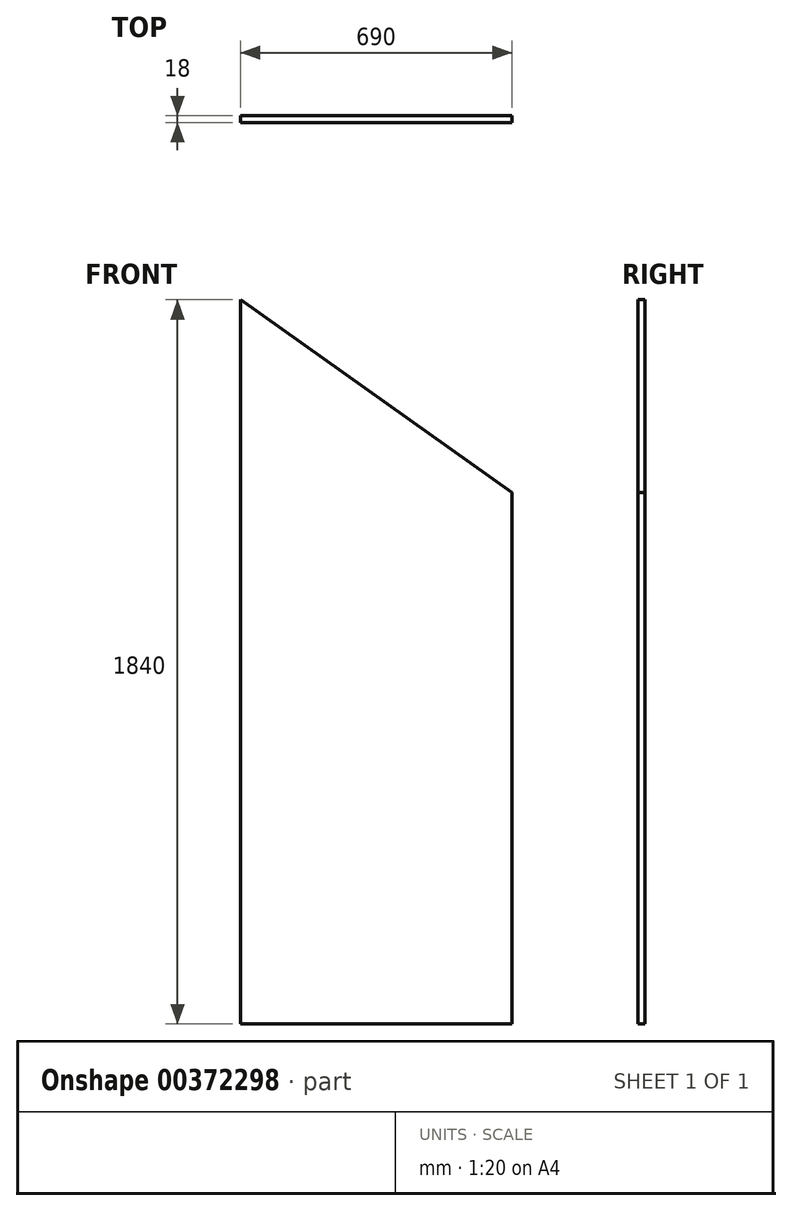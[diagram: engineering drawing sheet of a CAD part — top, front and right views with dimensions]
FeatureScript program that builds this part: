
annotation { "Feature Type Name" : "Feature", "Feature Type Description" : "" }
export const myFeature = defineFeature(function(context is Context, id is Id, definition is map)
    precondition{}
    {
        {
            var Q0;
            Q0=qCreatedBy(makeId("Front.planeOp"),FACE);
            var sketch = newSketch(context, id + "F0", { "sketchPlane" : qUnion([Q0])});
            skLineSegment(sketch, "E0", {"start": v(0, 0) * mm, "end": v(0, 1840) * mm});
            skLineSegment(sketch, "E1", {"start": v(0, 1840) * mm, "end": v(690, 1350) * mm});
            skLineSegment(sketch, "E2", {"start": v(690, 1350) * mm, "end": v(690, 0) * mm});
            skLineSegment(sketch, "E3", {"start": v(690, 0) * mm, "end": v(0, 0) * mm});
            skSolve(sketch);
        }
        {
            var Q0;
            Q0=makeQuery(id+"F0.imprint","IMPRINT",FACE,{"disambiguationData":[TD([[makeQuery(id+"F0.imprint","IMPRINT",EDGE,{"derivedFrom":sQuery(id+"F0.wireOp",EDGE,"E0")}),-1.0]])]});
            extrude(context, id + "F1", {"entities" : qUnion([Q0]), "depth" : 18 * mm});
        }
    });
